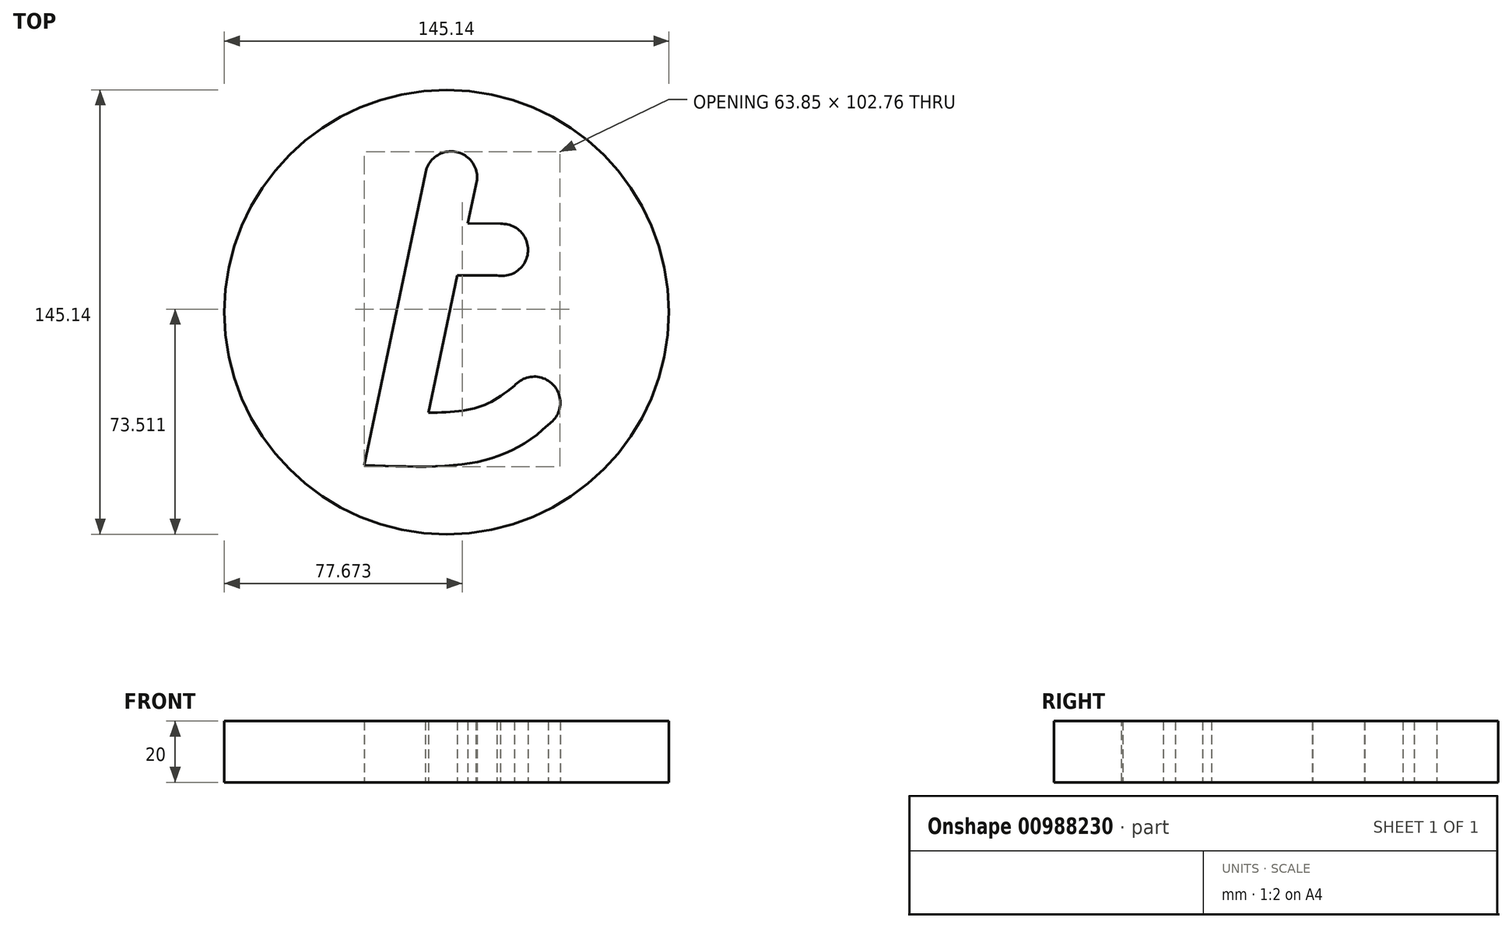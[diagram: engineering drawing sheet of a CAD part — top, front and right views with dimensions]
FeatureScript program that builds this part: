
annotation { "Feature Type Name" : "Feature", "Feature Type Description" : "" }
export const myFeature = defineFeature(function(context is Context, id is Id, definition is map)
    precondition{}
    {
        {
            var Q0;
            Q0=qCreatedBy(makeId("Top.planeOp"),FACE);
            var sketch = newSketch(context, id + "F0", { "sketchPlane" : qUnion([Q0])});
            skCircle(sketch, "E0", {"center": v(0, 0) * mm, "radius": 72.57 * mm});
            skArc(sketch, "E1", {"start": v(33.14, -36.77) * mm, "mid": v(35.06, -24.02) * mm, "end": v(22.16, -24.05) * mm});
            skArc(sketch, "E2", {"start": v(16.48, 11.99) * mm, "mid": v(26.57, 19.76) * mm, "end": v(17.62, 28.82) * mm});
            skArc(sketch, "E3", {"start": v(9.57, 41.46) * mm, "mid": v(3.3, 52.28) * mm, "end": v(-6.97, 45.13) * mm});
            skLineSegment(sketch, "E4", {"start": v(-6.72, 46.3) * mm, "end": v(-26.82, -50.01) * mm});
            skLineSegment(sketch, "E5", {"start": v(9.57, 41.46) * mm, "end": v(6.87, 29.01) * mm});
            skLineSegment(sketch, "E6", {"start": v(6.87, 29.01) * mm, "end": v(17.62, 28.82) * mm});
            skLineSegment(sketch, "E7", {"start": v(3.47, 11.99) * mm, "end": v(16.48, 11.99) * mm});
            skLineSegment(sketch, "E8", {"start": v(3.47, 11.99) * mm, "end": v(-5.86, -32.9) * mm});
            skFitSpline(sketch, "E9", {"points": [v(-5.86, -32.9) * mm, v(10.16, -31.12) * mm, v(22.16, -24.05) * mm], "startDerivative": vector(32.47, 0.52) * mm, "endDerivative": vector(27.71, 21.86) * mm});
            skFitSpline(sketch, "E10", {"points": [v(-26.82, -50.01) * mm, v(2.66, -50.01) * mm, v(19.54, -45.94) * mm, v(33.14, -36.77) * mm], "startDerivative": vector(79.01, -2.65) * mm, "endDerivative": vector(40.27, 40.87) * mm});
            skSolve(sketch);
        }
        {
            var Q0;
            Q0=makeQuery(id+"F0.imprint","IMPRINT",FACE,{"disambiguationData":[TD([[makeQuery(id+"F0.imprint","IMPRINT",EDGE,{"derivedFrom":sQuery(id+"F0.wireOp",EDGE,"E0")}),1.0]])]});
            extrude(context, id + "F1", {"entities" : qUnion([Q0]), "depth" : 20 * mm, "offsetDistance" : 25 * mm});
        }
    });
